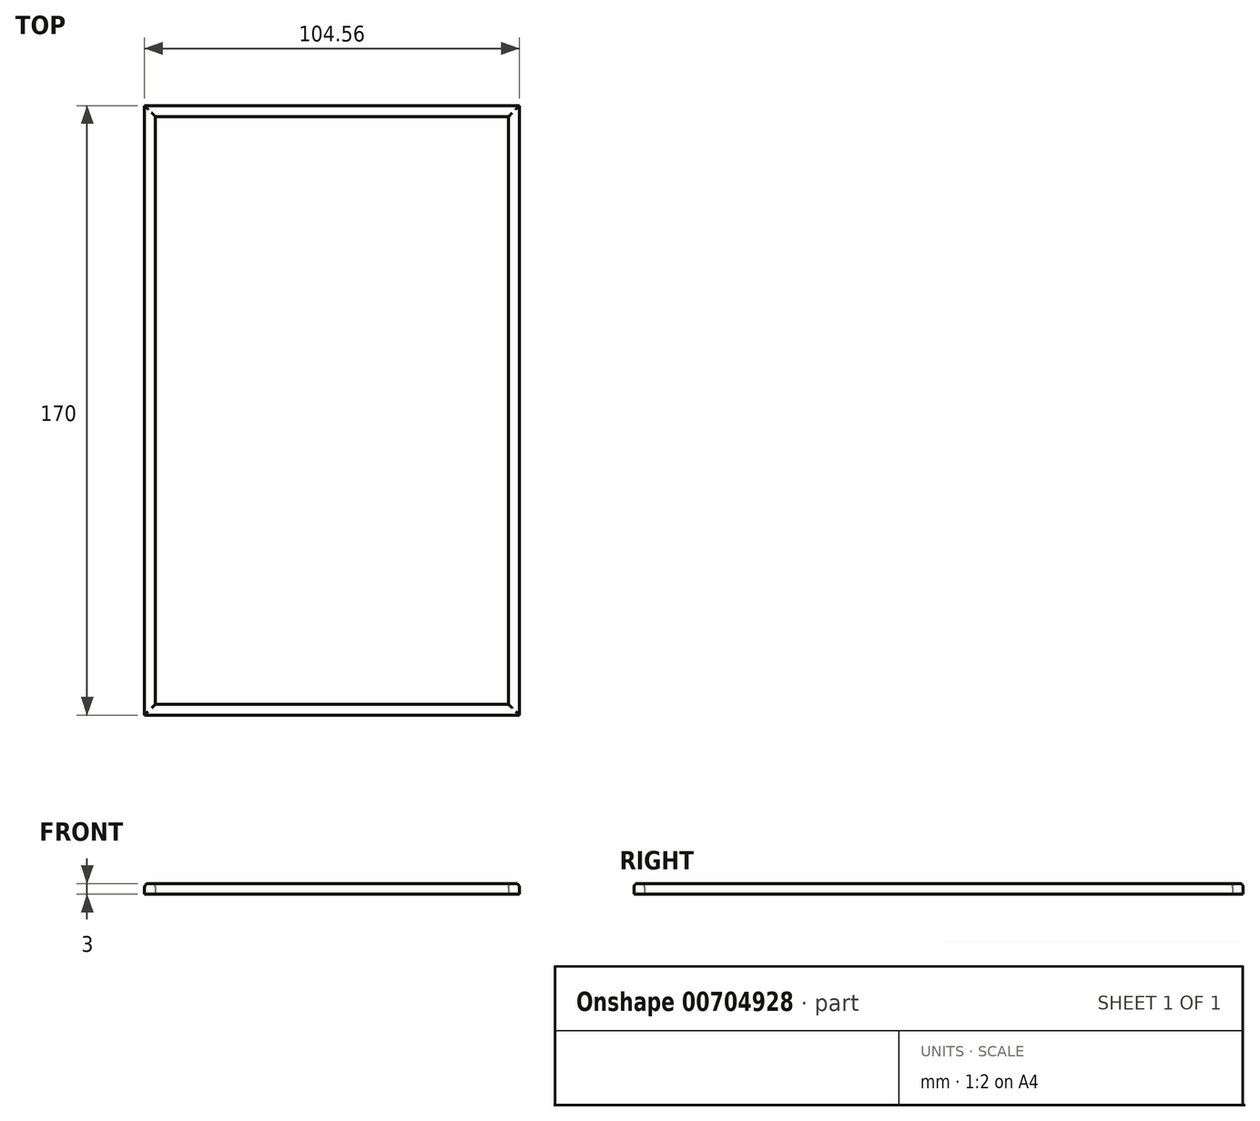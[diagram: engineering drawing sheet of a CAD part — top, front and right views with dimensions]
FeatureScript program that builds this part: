
annotation { "Feature Type Name" : "Feature", "Feature Type Description" : "" }
export const myFeature = defineFeature(function(context is Context, id is Id, definition is map)
    precondition{}
    {
        {
            var Q0;
            Q0=qCreatedBy(makeId("Top.planeOp"),FACE);
            var sketch = newSketch(context, id + "F0", { "sketchPlane" : qUnion([Q0])});
            skLineSegment(sketch, "E0", {"start": v(-52.28, -85) * mm, "end": v(52.28, -85) * mm});
            skLineSegment(sketch, "E1", {"start": v(52.28, -85) * mm, "end": v(52.28, 85) * mm});
            skLineSegment(sketch, "E2.MirrorCS", {"start": v(-52.28, 85) * mm, "end": v(52.28, 85) * mm});
            skLineSegment(sketch, "E3.MirrorCS", {"start": v(-52.28, -85) * mm, "end": v(-52.28, 85) * mm});
            skLineSegment(sketch, "E4.bottom", {"start": v(-49.28, -82) * mm, "end": v(49.28, -82) * mm});
            skLineSegment(sketch, "E4.top", {"start": v(-49.28, 82) * mm, "end": v(49.28, 82) * mm});
            skLineSegment(sketch, "E4.left", {"start": v(-49.28, -82) * mm, "end": v(-49.28, 82) * mm});
            skLineSegment(sketch, "E4.right", {"start": v(49.28, -82) * mm, "end": v(49.28, 82) * mm});
            skLineSegment(sketch, "E5.bottom", {"start": v(-55.78, 88.5) * mm, "end": v(55.78, 88.5) * mm, "construction": true});
            skLineSegment(sketch, "E5.top", {"start": v(-55.78, -88.5) * mm, "end": v(55.78, -88.5) * mm, "construction": true});
            skLineSegment(sketch, "E5.left", {"start": v(-55.78, 88.5) * mm, "end": v(-55.78, -88.5) * mm, "construction": true});
            skLineSegment(sketch, "E5.right", {"start": v(55.78, 88.5) * mm, "end": v(55.78, -88.5) * mm, "construction": true});
            skSolve(sketch);
        }
        {
            var Q0;
            Q0 = qSketchRegion(id + "F0", true);
            extrude(context, id + "F1", {"entities" : qUnion([Q0]), "depth" : 3 * mm, "offsetDistance" : 25 * mm});
        }
        {
            var Q0;
            Q0=makeQuery(id+"F1.opExtrude","CAP_EDGE",EDGE,{"disambiguationData":[OSD([sQuery(id+"F0.wireOp",EDGE,"E2.MirrorCS")])],"isStart":false});
            var Q1;
            Q1=makeQuery(id+"F1.opExtrude","CAP_EDGE",EDGE,{"disambiguationData":[OSD([sQuery(id+"F0.wireOp",EDGE,"E3.MirrorCS")])],"isStart":false});
            var Q2;
            Q2=makeQuery(id+"F1.opExtrude","CAP_EDGE",EDGE,{"disambiguationData":[OSD([sQuery(id+"F0.wireOp",EDGE,"E1")])],"isStart":false});
            var Q3;
            Q3=makeQuery(id+"F1.opExtrude","CAP_EDGE",EDGE,{"disambiguationData":[OSD([sQuery(id+"F0.wireOp",EDGE,"E4.right")])],"isStart":false});
            var Q4;
            Q4=makeQuery(id+"F1.opExtrude","CAP_EDGE",EDGE,{"disambiguationData":[OSD([sQuery(id+"F0.wireOp",EDGE,"E4.top")])],"isStart":false});
            var Q5;
            Q5=makeQuery(id+"F1.opExtrude","CAP_EDGE",EDGE,{"disambiguationData":[OSD([sQuery(id+"F0.wireOp",EDGE,"E4.left")])],"isStart":false});
            var Q6;
            Q6=makeQuery(id+"F1.opExtrude","CAP_EDGE",EDGE,{"disambiguationData":[OSD([sQuery(id+"F0.wireOp",EDGE,"E4.bottom")])],"isStart":false});
            var Q7;
            Q7=makeQuery(id+"F1.opExtrude","CAP_EDGE",EDGE,{"disambiguationData":[OSD([sQuery(id+"F0.wireOp",EDGE,"E0")])],"isStart":false});
            fillet(context, id + "F2", {"entities" : qUnion([Q0, Q1, Q2, Q3, Q4, Q5, Q6, Q7]), "radius" : 1 * mm, "tangentPropagation" : true, "allowEdgeOverflow" : false});
        }
    });
